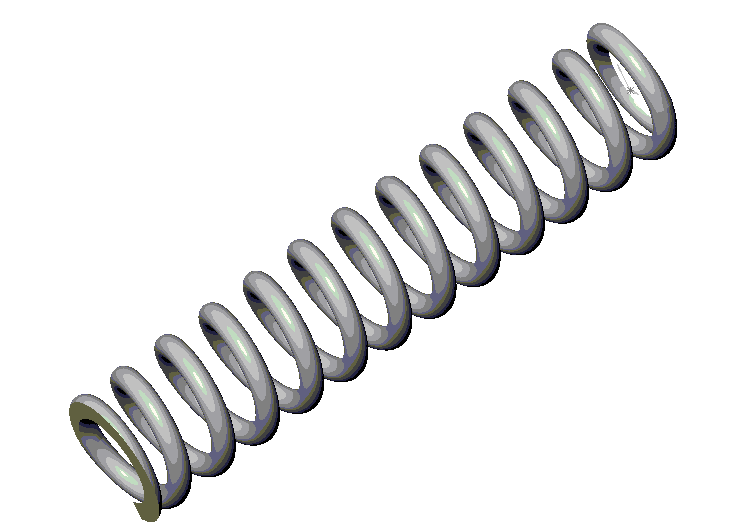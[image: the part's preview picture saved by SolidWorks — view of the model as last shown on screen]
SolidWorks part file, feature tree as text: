
SOLIDWORKS PART (.sldprt)
format: sldprt  version: not decoded by parser v0  size: 2,879,488 bytes
history: native  units: mm
features: sketch x8, plane x7, sweep x3, cut_extrude x2, material x1, helix x1 (+8 scaffold rows collapsed)
feature tree (30):
  scaffold x8  (default folders/planes/origin — collapsed)
  material  "Matériau <non spécifié>"
  plane  "Face"
  plane  "Dessus"
  plane  "Droite"
  sketch  "Esquisse1"  dims[D1=5.0mm]
  helix  "Hélice1"  Pitch=0mm
  plane  "Plan4"
  plane  "Plan5"
  sketch  "Esquisse2"  dims[D1=1.0mm]
  sketch  "Esquisse5"  dims[D1=5.0mm Hélice2=0.0 D3=0.7575mm D4=1.01mm D5=~42.971835deg]
  sketch  "Esquisse6"  dims[D1=5.0mm Hélice3=0.0 D3=0.7575mm D4=1.01mm D5=~42.971835deg D7=~3141.592654mm]
  sweep  "Base-Balayage"
  sketch  "Esquisse7"
  sweep  "Boss.-Balayage1"
  sketch  "Esquisse8"
  sweep  "Boss.-Balayage2"
  plane  "Plan8"  Offset=0.5mm
  sketch  "Esquisse9"  dims[D1=10.0mm]
  cut_extrude  "Enlèv. mat.-Extru.1"  [1 undecoded]
  plane  "Plan9"  Offset=0.5mm
  sketch  "Esquisse10"  dims[D1=10.0mm]
  cut_extrude  "Enlèv. mat.-Extru.2"  [1 undecoded]
decode coverage: 7 of 14 modeling features carry decoded parameters
note: ~ marks probable driven/reference dimensions
note: 2 parameter values undecoded
note: suppression state not decoded; provenance and decode notes live in map.json
